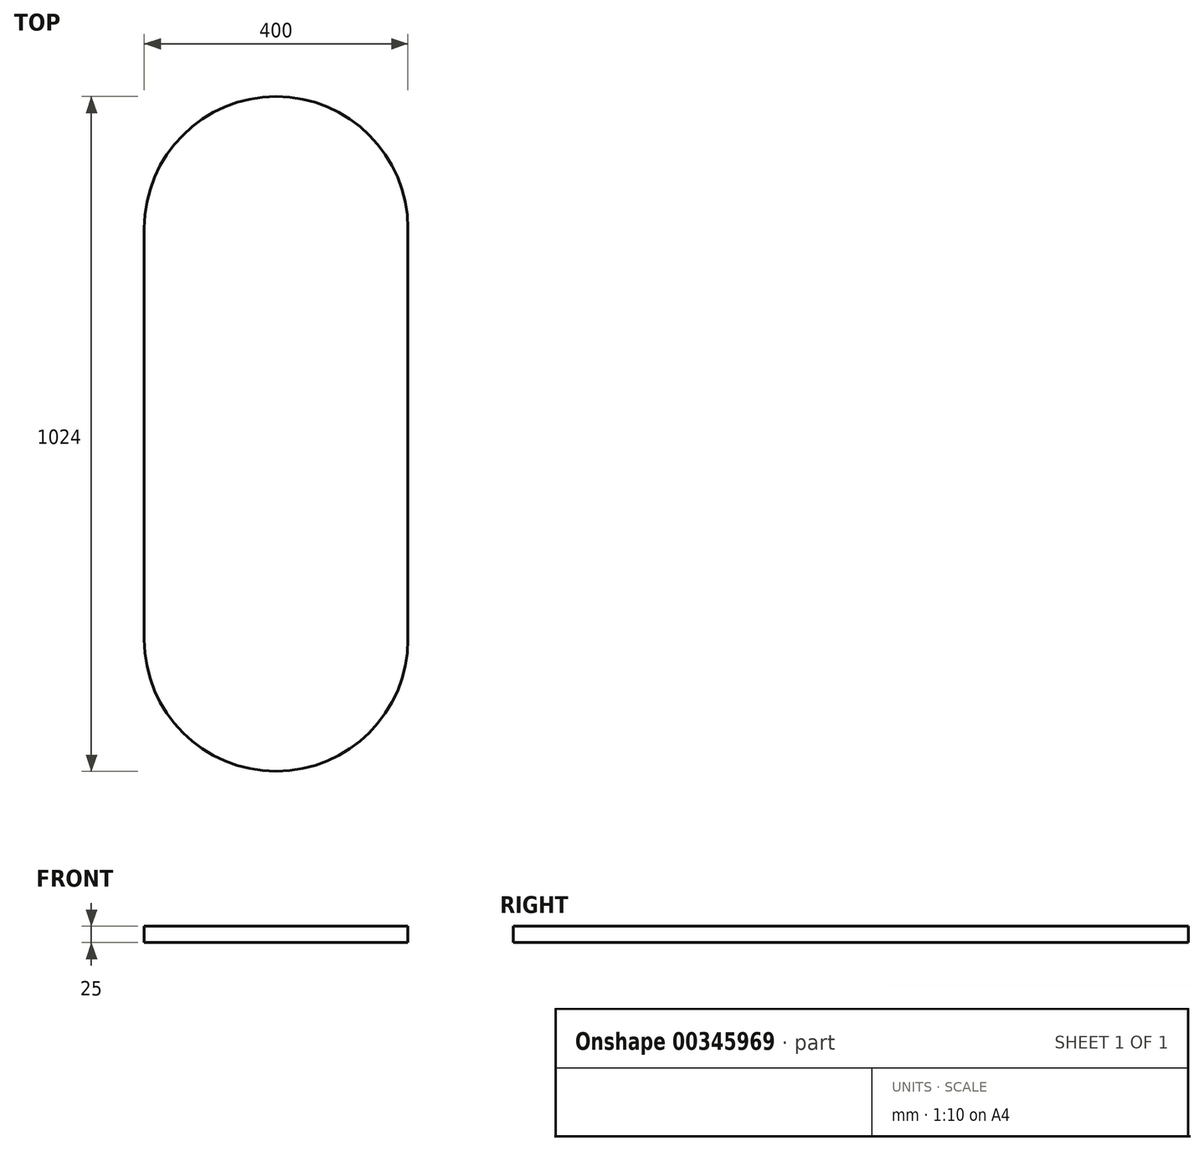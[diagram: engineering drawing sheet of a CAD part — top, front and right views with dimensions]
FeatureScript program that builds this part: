
annotation { "Feature Type Name" : "Feature", "Feature Type Description" : "" }
export const myFeature = defineFeature(function(context is Context, id is Id, definition is map)
    precondition{}
    {
        {
            var Q0;
            Q0=qCreatedBy(makeId("Top.planeOp"),FACE);
            var sketch = newSketch(context, id + "F0", { "sketchPlane" : qUnion([Q0])});
            skPoint(sketch, "E0", {"position": v(0, 312) * mm});
            skPoint(sketch, "E1", {"position": v(0, -312) * mm});
            skCircle(sketch, "E2", {"center": v(0, 312) * mm, "radius": 200 * mm});
            skCircle(sketch, "E3", {"center": v(0, -312) * mm, "radius": 200 * mm});
            skLineSegment(sketch, "E4", {"start": v(200, 312) * mm, "end": v(200, -312) * mm});
            skLineSegment(sketch, "E5", {"start": v(-200, 312) * mm, "end": v(-200, -312) * mm});
            skSolve(sketch);
        }
        {
            var Q0;
            {var subQ0=sQuery(id+"F0.wireOp",EDGE,"E2");var subQ1=makeQuery(id+"F0.imprint","INTERSECT",VERTEX,{"derivedFrom":[subQ0,sQuery(id+"F0.wireOp",EDGE,"E4")]});Q0=makeQuery(id+"F0.imprint","IMPRINT",FACE,{"disambiguationData":[TD([[makeQuery(id+"F0.imprint","IMPRINT",EDGE,{"disambiguationData":[TD([[subQ1,-1.0]])],"derivedFrom":subQ0}),1.0]])]});}
            var Q1;
            {var subQ0=sQuery(id+"F0.wireOp",EDGE,"E4");Q1=makeQuery(id+"F0.imprint","IMPRINT",FACE,{"disambiguationData":[TD([[makeQuery(id+"F0.imprint","IMPRINT",EDGE,{"derivedFrom":subQ0}),-1.0]])]});}
            var Q2;
            {var subQ0=sQuery(id+"F0.wireOp",EDGE,"E3");var subQ1=makeQuery(id+"F0.imprint","INTERSECT",VERTEX,{"derivedFrom":[subQ0,sQuery(id+"F0.wireOp",EDGE,"E4")]});Q2=makeQuery(id+"F0.imprint","IMPRINT",FACE,{"disambiguationData":[TD([[makeQuery(id+"F0.imprint","IMPRINT",EDGE,{"disambiguationData":[TD([[subQ1,-1.0]])],"derivedFrom":subQ0}),1.0]])]});}
            extrude(context, id + "F1", {"entities" : qUnion([Q0, Q1, Q2]), "depth" : 25 * mm});
        }
    });
